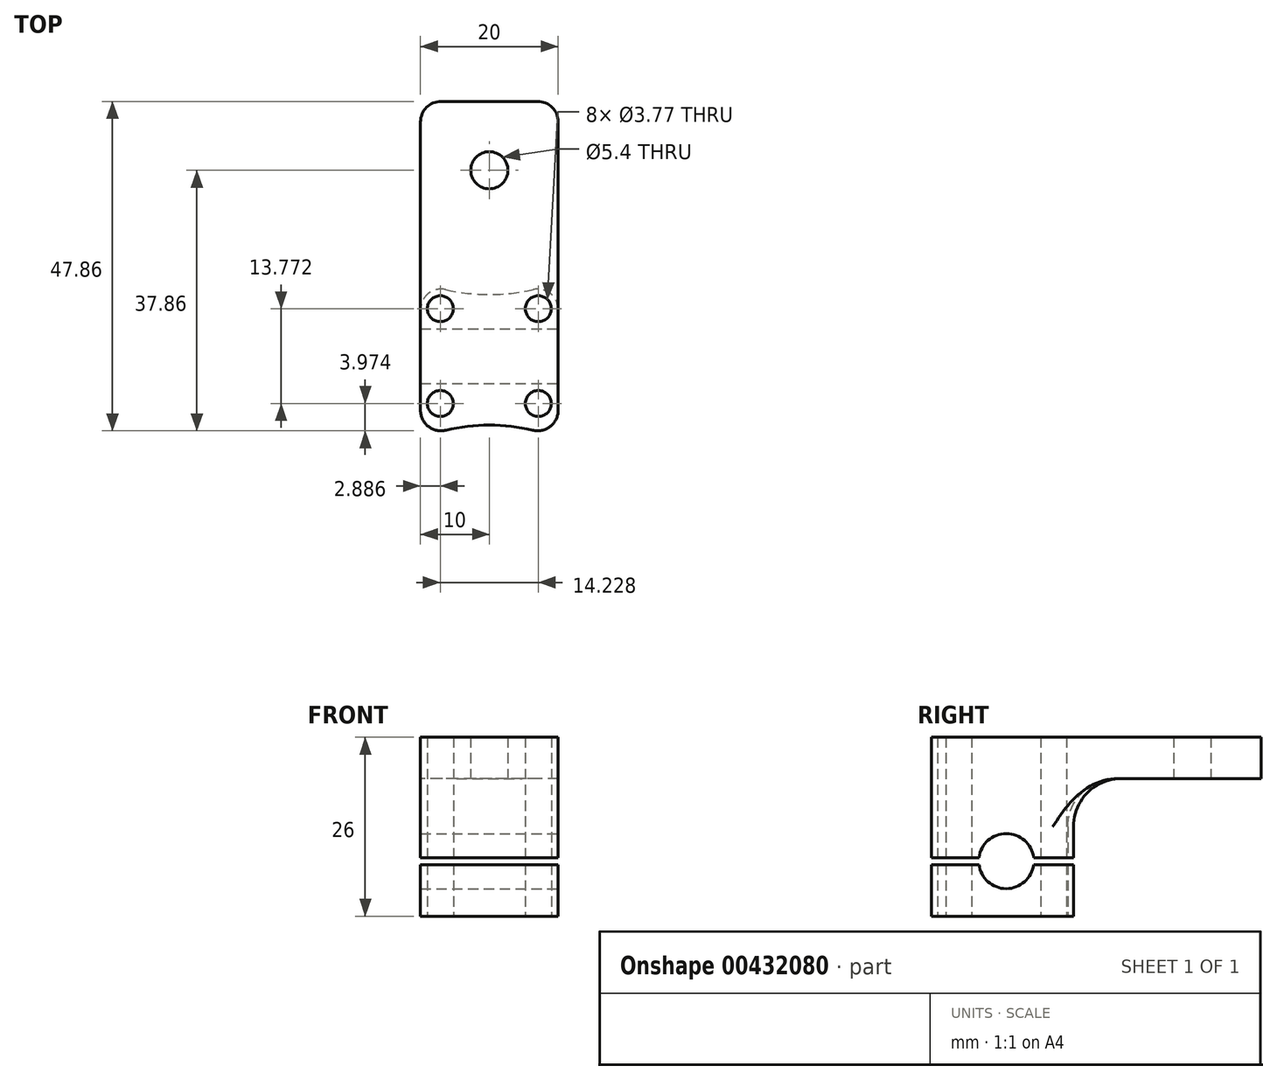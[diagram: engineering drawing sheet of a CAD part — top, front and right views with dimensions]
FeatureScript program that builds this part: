
annotation { "Feature Type Name" : "Feature", "Feature Type Description" : "" }
export const myFeature = defineFeature(function(context is Context, id is Id, definition is map)
    precondition{}
    {
        {
            var Q0;
            Q0=qCreatedBy(makeId("Top.planeOp"),FACE);
            var sketch = newSketch(context, id + "F0", { "sketchPlane" : qUnion([Q0])});
            skLineSegment(sketch, "E0.bottom", {"start": v(10, -24.5) * mm, "end": v(-10, -24.5) * mm});
            skLineSegment(sketch, "E0.top", {"start": v(10, 24.5) * mm, "end": v(-10, 24.5) * mm});
            skLineSegment(sketch, "E0.left", {"start": v(10, -24.5) * mm, "end": v(10, 24.5) * mm});
            skLineSegment(sketch, "E0.right", {"start": v(-10, -24.5) * mm, "end": v(-10, 24.5) * mm});
            skPoint(sketch, "E0.middle", {"position": v(0, 0) * mm});
            skLineSegment(sketch, "E1", {"start": v(-10, 4.5) * mm, "end": v(10, 4.5) * mm, "construction": true});
            skLineSegment(sketch, "E2", {"start": v(-10, -12.5) * mm, "end": v(10, -12.5) * mm, "construction": true});
            skCircle(sketch, "E3", {"center": v(-7.11, -5.61) * mm, "radius": 1.89 * mm});
            skLineSegment(sketch, "E4", {"start": v(-10, -8.5) * mm, "end": v(10, -8.5) * mm, "construction": true});
            skLineSegment(sketch, "E5", {"start": v(-10, -16.5) * mm, "end": v(10, -16.5) * mm, "construction": true});
            skCircle(sketch, "E6.MirrorC", {"center": v(7.11, -5.61) * mm, "radius": 1.89 * mm});
            skCircle(sketch, "E7.MirrorC", {"center": v(7.11, -19.39) * mm, "radius": 1.89 * mm});
            skCircle(sketch, "E8.MirrorC", {"center": v(-7.11, -19.39) * mm, "radius": 1.89 * mm});
            skCircle(sketch, "E9", {"center": v(0, 14.5) * mm, "radius": 2.7 * mm});
            skPoint(sketch, "E9.centerSnap0", {"position": v(0, 24.5) * mm});
            skLineSegment(sketch, "E10", {"start": v(10, -0.5) * mm, "end": v(-10, -0.5) * mm, "construction": true});
            skLineSegment(sketch, "E11", {"start": v(-10, -1.73) * mm, "end": v(10, -1.73) * mm});
            skSolve(sketch);
        }
        {
            var Q0;
            Q0=makeQuery(id+"F0.imprint","IMPRINT",FACE,{"disambiguationData":[TD([[makeQuery(id+"F0.imprint","IMPRINT",EDGE,{"derivedFrom":sQuery(id+"F0.wireOp",EDGE,"E0.bottom")}),-1.0]])]});
            var Q1;
            {var subQ1=sQuery(id+"F0.wireOp",EDGE,"E0.top");Q1=makeQuery(id+"F0.imprint","IMPRINT",FACE,{"disambiguationData":[TD([[makeQuery(id+"F0.imprint","IMPRINT",EDGE,{"derivedFrom":subQ1}),1.0]])]});}
            extrude(context, id + "F1", {"entities" : qUnion([Q0, Q1]), "depth" : 6 * mm});
        }
        {
            var Q0;
            {var subQ1=sQuery(id+"F0.wireOp",EDGE,"E0.bottom");Q0=makeQuery(id+"F0.imprint","IMPRINT",FACE,{"disambiguationData":[TD([[makeQuery(id+"F0.imprint","IMPRINT",EDGE,{"derivedFrom":subQ1}),-1.0]])]});}
            extrude(context, id + "F2", {"entities" : qUnion([Q0]), "operationType" : NewBodyOperationType.ADD, "oppositeDirection" : true, "depth" : 20 * mm});
        }
        {
            var Q0;
            {var subQ0=sQuery(id+"F0.wireOp",EDGE,"E0.left");Q0=makeQuery(id+"F2.boolean.opBoolean","MERGE",FACE,{"derivedFrom":[makeQuery(id+"F1.opExtrude","SWEPT_FACE",FACE,{"disambiguationData":[OSD([subQ0])]}),makeQuery(id+"F2.opExtrude","SWEPT_FACE",FACE,{"disambiguationData":[OSD([subQ0])]})]});}
            var sketch = newSketch(context, id + "F3", { "sketchPlane" : qUnion([Q0])});
            skCircle(sketch, "E12", {"center": v(-12.5, -12) * mm, "radius": 4 * mm});
            skLineSegment(sketch, "E13", {"start": v(-1.73, -12) * mm, "end": v(-24.5, -12) * mm, "construction": true});
            skLineSegment(sketch, "E14.bottom", {"start": v(-1.73, -12) * mm, "end": v(-24.5, -12) * mm});
            skLineSegment(sketch, "E14.top", {"start": v(-1.73, -11.5) * mm, "end": v(-24.5, -11.5) * mm});
            skLineSegment(sketch, "E14.left", {"start": v(-1.73, -12) * mm, "end": v(-1.73, -11.5) * mm});
            skLineSegment(sketch, "E14.right", {"start": v(-24.5, -12) * mm, "end": v(-24.5, -11.5) * mm});
            skLineSegment(sketch, "E15.MirrorCS", {"start": v(-1.73, -12.5) * mm, "end": v(-24.5, -12.5) * mm});
            skLineSegment(sketch, "E16.MirrorCS", {"start": v(-1.73, -12) * mm, "end": v(-1.73, -12.5) * mm});
            skLineSegment(sketch, "E17.MirrorCS", {"start": v(-24.5, -12) * mm, "end": v(-24.5, -12.5) * mm});
            skSolve(sketch);
        }
        {
            var Q0;
            Q0=makeQuery(id+"F3.imprint","IMPRINT",FACE,{"disambiguationData":[TD([[makeQuery(id+"F3.imprint","IMPRINT",EDGE,{"derivedFrom":sQuery(id+"F3.wireOp",EDGE,"E12")}),1.0]])]});
            var Q1;
            {var subQ0=sQuery(id+"F3.wireOp",EDGE,"E14.top");var subQ1=sQuery(id+"F3.wireOp",EDGE,"E12");var subQ2=makeQuery(id+"F3.imprint","INTERSECT",VERTEX,{"disambiguationData":[OD(0.0)],"derivedFrom":[subQ1,subQ0]});Q1=makeQuery(id+"F3.imprint","IMPRINT",FACE,{"disambiguationData":[TD([[makeQuery(id+"F3.imprint","IMPRINT",EDGE,{"disambiguationData":[TD([[subQ2,1.0]])],"derivedFrom":subQ1}),1.0]])]});}
            var Q2;
            {var subQ0=sQuery(id+"F3.wireOp",EDGE,"E15.MirrorCS");var subQ1=sQuery(id+"F3.wireOp",EDGE,"E12");var subQ2=makeQuery(id+"F3.imprint","INTERSECT",VERTEX,{"disambiguationData":[OD(0.0)],"derivedFrom":[subQ1,subQ0]});Q2=makeQuery(id+"F3.imprint","IMPRINT",FACE,{"disambiguationData":[TD([[makeQuery(id+"F3.imprint","IMPRINT",EDGE,{"disambiguationData":[TD([[subQ2,-1.0]])],"derivedFrom":subQ1}),1.0]])]});}
            extrude(context, id + "F4", {"entities" : qUnion([Q0, Q1, Q2]), "operationType" : NewBodyOperationType.REMOVE, "endBound" : BoundingType.THROUGH_ALL, "oppositeDirection" : true, "depth" : 25 * mm});
        }
        {
            var Q0;
            Q0=makeQuery(id+"F2.opExtrude","CAP_FACE",FACE,{"disambiguationData":[OSD([sQuery(id+"F0.wireOp",EDGE,"E0.bottom"),sQuery(id+"F0.wireOp",EDGE,"E0.left"),sQuery(id+"F0.wireOp",EDGE,"E0.right"),sQuery(id+"F0.wireOp",EDGE,"E3"),sQuery(id+"F0.wireOp",EDGE,"E6.MirrorC"),sQuery(id+"F0.wireOp",EDGE,"E7.MirrorC"),sQuery(id+"F0.wireOp",EDGE,"E8.MirrorC"),sQuery(id+"F0.wireOp",EDGE,"E11")])],"isStart":false});
            var sketch = newSketch(context, id + "F5", { "sketchPlane" : qUnion([Q0])});
            skArc(sketch, "E18", {"start": v(10, 1.73) * mm, "mid": v(0, 3.55) * mm, "end": v(-10, 1.73) * mm});
            skArc(sketch, "E19", {"start": v(-10, 24.5) * mm, "mid": v(0, 22.5) * mm, "end": v(10, 24.5) * mm});
            skSolve(sketch);
        }
        {
            var Q0;
            Q0=makeQuery(id+"F5.imprint","IMPRINT",FACE,{"disambiguationData":[TD([[makeQuery(id+"F5.imprint","IMPRINT",EDGE,{"derivedFrom":sQuery(id+"F5.wireOp",EDGE,"E18")}),1.0]])]});
            var Q1;
            Q1=makeQuery(id+"F1.opExtrude","CAP_FACE",FACE,{"disambiguationData":[OSD([sQuery(id+"F0.wireOp",EDGE,"E0.bottom"),sQuery(id+"F0.wireOp",EDGE,"E0.top"),sQuery(id+"F0.wireOp",EDGE,"E0.left"),sQuery(id+"F0.wireOp",EDGE,"E0.right"),sQuery(id+"F0.wireOp",EDGE,"E3"),sQuery(id+"F0.wireOp",EDGE,"E6.MirrorC"),sQuery(id+"F0.wireOp",EDGE,"E7.MirrorC"),sQuery(id+"F0.wireOp",EDGE,"E8.MirrorC"),sQuery(id+"F0.wireOp",EDGE,"E9")])],"isStart":true});
            extrude(context, id + "F6", {"entities" : qUnion([Q0]), "operationType" : NewBodyOperationType.REMOVE, "endBound" : BoundingType.UP_TO_SURFACE, "oppositeDirection" : true, "endBoundEntityFace" : qUnion([Q1]), "depth" : 25 * mm});
        }
        {
            var Q0;
            Q0=makeQuery(id+"F5.imprint","IMPRINT",FACE,{"disambiguationData":[TD([[makeQuery(id+"F5.imprint","IMPRINT",EDGE,{"derivedFrom":sQuery(id+"F5.wireOp",EDGE,"E19")}),1.0]])]});
            extrude(context, id + "F7", {"entities" : qUnion([Q0]), "operationType" : NewBodyOperationType.REMOVE, "endBound" : BoundingType.THROUGH_ALL, "oppositeDirection" : true, "depth" : 25 * mm});
        }
        {
            var Q0;
            Q0=makeQuery(id+"F1.opExtrude","SWEPT_EDGE",EDGE,{"disambiguationData":[OSD([sQuery(id+"F0.wireOp",EDGE,"E0.top"),sQuery(id+"F0.wireOp",EDGE,"E0.right")])]});
            var Q1;
            Q1=makeQuery(id+"F1.opExtrude","SWEPT_EDGE",EDGE,{"disambiguationData":[OSD([sQuery(id+"F0.wireOp",EDGE,"E0.top"),sQuery(id+"F0.wireOp",EDGE,"E0.left")])]});
            var Q2;
            {var subQ0=sQuery(id+"F0.wireOp",EDGE,"E0.left");var subQ1=sQuery(id+"F0.wireOp",EDGE,"E0.bottom");Q2=makeQuery(id+"F7.boolean.opBoolean","MERGE",EDGE,{"derivedFrom":[makeQuery(id+"F2.boolean.opBoolean","MERGE",EDGE,{"derivedFrom":[makeQuery(id+"F1.opExtrude","SWEPT_EDGE",EDGE,{"disambiguationData":[OSD([subQ1,subQ0])]}),makeQuery(id+"F2.opExtrude","SWEPT_EDGE",EDGE,{"disambiguationData":[OSD([subQ1,subQ0])]})]}),makeQuery(id+"F7.opExtrude","SWEPT_EDGE",EDGE,{"disambiguationData":[OSD([subQ1,subQ0,sQuery(id+"F5.wireOp",EDGE,"E19")])]})]});}
            var Q3;
            {var subQ0=sQuery(id+"F0.wireOp",EDGE,"E0.right");var subQ1=sQuery(id+"F0.wireOp",EDGE,"E0.bottom");Q3=makeQuery(id+"F7.boolean.opBoolean","MERGE",EDGE,{"derivedFrom":[makeQuery(id+"F2.boolean.opBoolean","MERGE",EDGE,{"derivedFrom":[makeQuery(id+"F1.opExtrude","SWEPT_EDGE",EDGE,{"disambiguationData":[OSD([subQ1,subQ0])]}),makeQuery(id+"F2.opExtrude","SWEPT_EDGE",EDGE,{"disambiguationData":[OSD([subQ1,subQ0])]})]}),makeQuery(id+"F7.opExtrude","SWEPT_EDGE",EDGE,{"disambiguationData":[OSD([subQ1,subQ0,sQuery(id+"F5.wireOp",EDGE,"E19")])]})]});}
            var Q4;
            {var subQ0=sQuery(id+"F0.wireOp",EDGE,"E11");var subQ1=sQuery(id+"F0.wireOp",EDGE,"E0.right");Q4=makeQuery(id+"F6.boolean.opBoolean","MERGE",EDGE,{"derivedFrom":[makeQuery(id+"F2.opExtrude","SWEPT_EDGE",EDGE,{"disambiguationData":[OSD([subQ1,subQ0])]})],"fromTools":[makeQuery(id+"F6.opExtrude","SWEPT_EDGE",EDGE,{"disambiguationData":[OSD([subQ1,subQ0,sQuery(id+"F5.wireOp",EDGE,"E18")])]})]});}
            var Q5;
            {var subQ0=sQuery(id+"F0.wireOp",EDGE,"E11");var subQ1=sQuery(id+"F0.wireOp",EDGE,"E0.left");Q5=makeQuery(id+"F6.boolean.opBoolean","MERGE",EDGE,{"derivedFrom":[makeQuery(id+"F2.opExtrude","SWEPT_EDGE",EDGE,{"disambiguationData":[OSD([subQ1,subQ0])]})],"fromTools":[makeQuery(id+"F6.opExtrude","SWEPT_EDGE",EDGE,{"disambiguationData":[OSD([subQ1,subQ0,sQuery(id+"F5.wireOp",EDGE,"E18")])]})]});}
            fillet(context, id + "F8", {"entities" : qUnion([Q0, Q1, Q2, Q3, Q4, Q5]), "radius" : 3 * mm, "tangentPropagation" : true, "allowEdgeOverflow" : false});
        }
        {
            var Q0;
            Q0=makeQuery(id+"F6.boolean.opBoolean","COPY",EDGE,{"derivedFrom":makeQuery(id+"F6.opExtrude","CAP_EDGE",EDGE,{"disambiguationData":[OSD([sQuery(id+"F5.wireOp",EDGE,"E18")])],"isStart":false})});
            fillet(context, id + "F9", {"entities" : qUnion([Q0]), "radius" : 7 * mm, "tangentPropagation" : true, "allowEdgeOverflow" : false});
        }
        {
            var Q0;
            {var subQ5=sQuery(id+"F3.wireOp",EDGE,"E17.MirrorCS");Q0=makeQuery(id+"F3.imprint","IMPRINT",FACE,{"disambiguationData":[TD([[makeQuery(id+"F3.imprint","IMPRINT",EDGE,{"derivedFrom":subQ5}),1.0]])]});}
            var Q1;
            {var subQ5=sQuery(id+"F3.wireOp",EDGE,"E14.right");Q1=makeQuery(id+"F3.imprint","IMPRINT",FACE,{"disambiguationData":[TD([[makeQuery(id+"F3.imprint","IMPRINT",EDGE,{"derivedFrom":subQ5}),1.0]])]});}
            var Q2;
            {var subQ0=sQuery(id+"F3.wireOp",EDGE,"E14.bottom");var subQ1=sQuery(id+"F3.wireOp",EDGE,"E12");var subQ2=makeQuery(id+"F3.imprint","INTERSECT",VERTEX,{"disambiguationData":[OD(0.0)],"derivedFrom":[subQ1,subQ0]});Q2=makeQuery(id+"F3.imprint","IMPRINT",FACE,{"disambiguationData":[TD([[makeQuery(id+"F3.imprint","IMPRINT",EDGE,{"disambiguationData":[TD([[subQ2,-1.0]])],"derivedFrom":subQ1}),1.0]])]});}
            var Q3;
            {var subQ0=sQuery(id+"F3.wireOp",EDGE,"E14.top");var subQ1=sQuery(id+"F3.wireOp",EDGE,"E12");var subQ2=makeQuery(id+"F3.imprint","INTERSECT",VERTEX,{"disambiguationData":[OD(0.0)],"derivedFrom":[subQ1,subQ0]});Q3=makeQuery(id+"F3.imprint","IMPRINT",FACE,{"disambiguationData":[TD([[makeQuery(id+"F3.imprint","IMPRINT",EDGE,{"disambiguationData":[TD([[subQ2,-1.0]])],"derivedFrom":subQ1}),1.0]])]});}
            var Q4;
            {var subQ5=sQuery(id+"F3.wireOp",EDGE,"E14.left");Q4=makeQuery(id+"F3.imprint","IMPRINT",FACE,{"disambiguationData":[TD([[makeQuery(id+"F3.imprint","IMPRINT",EDGE,{"derivedFrom":subQ5}),1.0]])]});}
            var Q5;
            {var subQ5=sQuery(id+"F3.wireOp",EDGE,"E16.MirrorCS");Q5=makeQuery(id+"F3.imprint","IMPRINT",FACE,{"disambiguationData":[TD([[makeQuery(id+"F3.imprint","IMPRINT",EDGE,{"derivedFrom":subQ5}),1.0]])]});}
            extrude(context, id + "F10", {"entities" : qUnion([Q0, Q1, Q2, Q3, Q4, Q5]), "operationType" : NewBodyOperationType.REMOVE, "endBound" : BoundingType.THROUGH_ALL, "oppositeDirection" : true, "depth" : 25 * mm});
        }
    });
